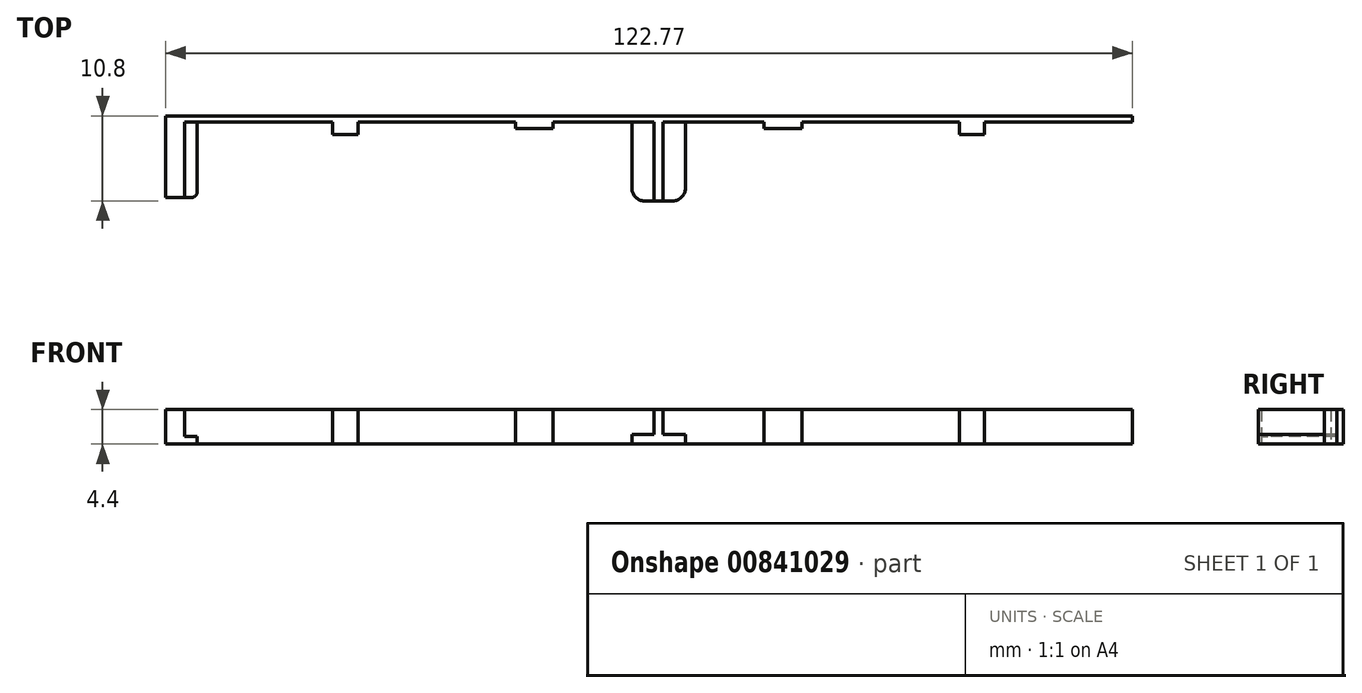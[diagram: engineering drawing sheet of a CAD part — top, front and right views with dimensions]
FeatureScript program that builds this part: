
annotation { "Feature Type Name" : "Feature", "Feature Type Description" : "" }
export const myFeature = defineFeature(function(context is Context, id is Id, definition is map)
    precondition{}
    {
        {
            var Q0;
            Q0=qCreatedBy(makeId("Top.planeOp"),FACE);
            var sketch = newSketch(context, id + "F0", { "sketchPlane" : qUnion([Q0])});
            skLineSegment(sketch, "E0", {"start": v(-62.6, 5.4) * mm, "end": v(62.6, 5.4) * mm});
            skLineSegment(sketch, "E1.top", {"start": v(-59.4, -4.2) * mm, "end": v(-62.6, -4.2) * mm});
            skLineSegment(sketch, "E1.left", {"start": v(-58.6, 6.2) * mm, "end": v(-58.6, -4.2) * mm});
            skLineSegment(sketch, "E1.right", {"start": v(-62.6, 6.2) * mm, "end": v(-62.6, -4.2) * mm});
            skLineSegment(sketch, "E2.bottom", {"start": v(-41.4, 5.4) * mm, "end": v(-38.2, 5.4) * mm});
            skLineSegment(sketch, "E2.top", {"start": v(-41.4, 3.8) * mm, "end": v(-38.2, 3.8) * mm});
            skLineSegment(sketch, "E2.left", {"start": v(-41.4, 5.4) * mm, "end": v(-41.4, 3.8) * mm});
            skLineSegment(sketch, "E2.right", {"start": v(-38.2, 5.4) * mm, "end": v(-38.2, 3.8) * mm});
            skLineSegment(sketch, "E3.bottom", {"start": v(-18.2, 5.4) * mm, "end": v(-13.4, 5.4) * mm});
            skLineSegment(sketch, "E3.top", {"start": v(-18.2, 4.6) * mm, "end": v(-13.4, 4.6) * mm});
            skLineSegment(sketch, "E3.left", {"start": v(-18.2, 5.4) * mm, "end": v(-18.2, 4.6) * mm});
            skLineSegment(sketch, "E3.right", {"start": v(-13.4, 5.4) * mm, "end": v(-13.4, 4.6) * mm});
            skLineSegment(sketch, "E4.bottom", {"start": v(3.4, 5.4) * mm, "end": v(-3.4, 5.4) * mm});
            skLineSegment(sketch, "E4.top", {"start": v(1.8, -4.6) * mm, "end": v(-1.8, -4.6) * mm});
            skLineSegment(sketch, "E4.left", {"start": v(3.4, 5.4) * mm, "end": v(3.4, -3) * mm});
            skLineSegment(sketch, "E4.right", {"start": v(-3.4, 5.4) * mm, "end": v(-3.4, -3) * mm});
            skPoint(sketch, "E4.middle", {"position": v(0, 0.4) * mm});
            skLineSegment(sketch, "E5.0", {"start": v(-60.2, 6.2) * mm, "end": v(-60.2, -4.2) * mm});
            skLineSegment(sketch, "E6", {"start": v(-62.6, 6.2) * mm, "end": v(62.6, 6.2) * mm});
            skPoint(sketch, "E7.visualSharp", {"position": v(-3.4, -4.6) * mm});
            skArc(sketch, "E7.filletArc", {"start": v(-3.4, -3) * mm, "mid": v(-2.93, -4.13) * mm, "end": v(-1.8, -4.6) * mm});
            skPoint(sketch, "E8.visualSharp", {"position": v(3.4, -4.6) * mm});
            skArc(sketch, "E8.filletArc", {"start": v(1.8, -4.6) * mm, "mid": v(2.93, -4.13) * mm, "end": v(3.4, -3) * mm});
            skLineSegment(sketch, "E9.0.left", {"start": v(-0.6, -4.6) * mm, "end": v(-0.6, 5.4) * mm});
            skLineSegment(sketch, "E9.0.right", {"start": v(0.6, -4.6) * mm, "end": v(0.6, 5.4) * mm});
            skArc(sketch, "E10.filletArc", {"start": v(-59.4, -4.2) * mm, "mid": v(-58.83, -3.97) * mm, "end": v(-58.6, -3.4) * mm});
            skLineSegment(sketch, "E11", {"start": v(62.6, 5.4) * mm, "end": v(62.6, 5.8) * mm});
            skLineSegment(sketch, "E12", {"start": v(62.6, 5.8) * mm, "end": v(62.6, 5.8) * mm});
            skLineSegment(sketch, "E13.MirrorCS", {"start": v(18.2, 4.6) * mm, "end": v(13.4, 4.6) * mm});
            skLineSegment(sketch, "E14.MirrorCS", {"start": v(18.2, 5.4) * mm, "end": v(18.2, 4.6) * mm});
            skLineSegment(sketch, "E15.MirrorCS", {"start": v(13.4, 5.4) * mm, "end": v(13.4, 4.6) * mm});
            skLineSegment(sketch, "E16.MirrorCS", {"start": v(38.2, 5.4) * mm, "end": v(38.2, 3.8) * mm});
            skLineSegment(sketch, "E17.MirrorCS", {"start": v(41.4, 5.4) * mm, "end": v(41.4, 3.8) * mm});
            skLineSegment(sketch, "E18.MirrorCS", {"start": v(41.4, 3.8) * mm, "end": v(38.2, 3.8) * mm});
            skLineSegment(sketch, "E19.MirrorCS", {"start": v(58.6, 6.2) * mm, "end": v(58.6, -4.2) * mm});
            skLineSegment(sketch, "E20.MirrorCS", {"start": v(60.17, 6.2) * mm, "end": v(60.2, -4.2) * mm});
            skLineSegment(sketch, "E21.MirrorCS", {"start": v(62.6, 6.2) * mm, "end": v(62.6, -4.2) * mm});
            skLineSegment(sketch, "E22.MirrorCS", {"start": v(59.4, -4.2) * mm, "end": v(62.6, -4.2) * mm});
            skArc(sketch, "E23.MirrorCS", {"start": v(59.4, -4.2) * mm, "mid": v(58.83, -3.97) * mm, "end": v(58.6, -3.4) * mm});
            skSolve(sketch);
        }
        {
            var Q0;
            {var subQ0=sQuery(id+"F0.wireOp",EDGE,"E1.right");var subQ1=sQuery(id+"F0.wireOp",EDGE,"E0");var subQ2=makeQuery(id+"F0.imprint","INTERSECT",VERTEX,{"derivedFrom":[subQ1,subQ0]});Q0=makeQuery(id+"F0.imprint","IMPRINT",FACE,{"disambiguationData":[TD([[makeQuery(id+"F0.imprint","IMPRINT",EDGE,{"disambiguationData":[TD([[subQ2,-1.0]])],"derivedFrom":subQ1}),-1.0]])]});}
            var Q1;
            {var subQ0=sQuery(id+"F0.wireOp",EDGE,"E1.right");var subQ1=sQuery(id+"F0.wireOp",EDGE,"E0");var subQ2=makeQuery(id+"F0.imprint","INTERSECT",VERTEX,{"derivedFrom":[subQ1,subQ0]});Q1=makeQuery(id+"F0.imprint","IMPRINT",FACE,{"disambiguationData":[TD([[makeQuery(id+"F0.imprint","IMPRINT",EDGE,{"disambiguationData":[TD([[subQ2,-1.0]])],"derivedFrom":subQ1}),1.0]])]});}
            var Q2;
            {var subQ17=sQuery(id+"F0.wireOp",EDGE,"E2.bottom");Q2=makeQuery(id+"F0.imprint","IMPRINT",FACE,{"disambiguationData":[TD([[makeQuery(id+"F0.imprint","IMPRINT",EDGE,{"derivedFrom":subQ17}),1.0]])]});}
            var Q3;
            {var subQ0=sQuery(id+"F0.wireOp",EDGE,"E21.MirrorCS");var subQ1=sQuery(id+"F0.wireOp",EDGE,"E0");var subQ2=makeQuery(id+"F0.imprint","INTERSECT",VERTEX,{"derivedFrom":[subQ1,subQ0]});Q3=makeQuery(id+"F0.imprint","IMPRINT",FACE,{"disambiguationData":[TD([[makeQuery(id+"F0.imprint","IMPRINT",EDGE,{"disambiguationData":[TD([[subQ2,1.0]])],"derivedFrom":subQ1}),1.0]])]});}
            var Q4;
            {var subQ0=sQuery(id+"F0.wireOp",EDGE,"E21.MirrorCS");var subQ1=sQuery(id+"F0.wireOp",EDGE,"E0");var subQ2=makeQuery(id+"F0.imprint","INTERSECT",VERTEX,{"derivedFrom":[subQ1,subQ0]});Q4=makeQuery(id+"F0.imprint","IMPRINT",FACE,{"disambiguationData":[TD([[makeQuery(id+"F0.imprint","IMPRINT",EDGE,{"disambiguationData":[TD([[subQ2,1.0]])],"derivedFrom":subQ1}),-1.0]])]});}
            var Q5;
            {var subQ0=sQuery(id+"F0.wireOp",EDGE,"E9.0.left");Q5=makeQuery(id+"F0.imprint","IMPRINT",FACE,{"disambiguationData":[TD([[makeQuery(id+"F0.imprint","IMPRINT",EDGE,{"derivedFrom":subQ0}),-1.0]])]});}
            var Q6;
            {var subQ0=sQuery(id+"F0.wireOp",EDGE,"E1.left");var subQ1=sQuery(id+"F0.wireOp",EDGE,"E0");var subQ2=makeQuery(id+"F0.imprint","INTERSECT",VERTEX,{"derivedFrom":[subQ1,subQ0]});Q6=makeQuery(id+"F0.imprint","IMPRINT",FACE,{"disambiguationData":[TD([[makeQuery(id+"F0.imprint","IMPRINT",EDGE,{"disambiguationData":[TD([[subQ2,1.0]])],"derivedFrom":subQ1}),1.0]])]});}
            var Q7;
            {var subQ0=sQuery(id+"F0.wireOp",EDGE,"E19.MirrorCS");var subQ1=sQuery(id+"F0.wireOp",EDGE,"E0");var subQ2=makeQuery(id+"F0.imprint","INTERSECT",VERTEX,{"derivedFrom":[subQ1,subQ0]});Q7=makeQuery(id+"F0.imprint","IMPRINT",FACE,{"disambiguationData":[TD([[makeQuery(id+"F0.imprint","IMPRINT",EDGE,{"disambiguationData":[TD([[subQ2,-1.0]])],"derivedFrom":subQ1}),1.0]])]});}
            extrude(context, id + "F1", {"entities" : qUnion([Q0, Q1, Q2, Q3, Q4, Q5, Q6, Q7]), "depth" : 4.4 * mm, "offsetDistance" : 25 * mm});
        }
        {
            var Q0;
            {var subQ0=sQuery(id+"F0.wireOp",EDGE,"E16.MirrorCS");Q0=makeQuery(id+"F0.imprint","IMPRINT",FACE,{"disambiguationData":[TD([[makeQuery(id+"F0.imprint","IMPRINT",EDGE,{"derivedFrom":subQ0}),1.0]])]});}
            var Q1;
            Q1=makeQuery(id+"F0.imprint","IMPRINT",FACE,{"disambiguationData":[TD([[makeQuery(id+"F0.imprint","IMPRINT",EDGE,{"derivedFrom":sQuery(id+"F0.wireOp",EDGE,"E13.MirrorCS")}),-1.0]])]});
            var Q2;
            {var subQ0=sQuery(id+"F0.wireOp",EDGE,"E4.left");Q2=makeQuery(id+"F0.imprint","IMPRINT",FACE,{"disambiguationData":[TD([[makeQuery(id+"F0.imprint","IMPRINT",EDGE,{"derivedFrom":subQ0}),-1.0]])]});}
            var Q3;
            {var subQ3=sQuery(id+"F0.wireOp",EDGE,"E4.right");Q3=makeQuery(id+"F0.imprint","IMPRINT",FACE,{"disambiguationData":[TD([[makeQuery(id+"F0.imprint","IMPRINT",EDGE,{"derivedFrom":subQ3}),1.0]])]});}
            var Q4;
            Q4=makeQuery(id+"F0.imprint","IMPRINT",FACE,{"disambiguationData":[TD([[makeQuery(id+"F0.imprint","IMPRINT",EDGE,{"derivedFrom":sQuery(id+"F0.wireOp",EDGE,"E3.bottom")}),-1.0]])]});
            var Q5;
            Q5=makeQuery(id+"F0.imprint","IMPRINT",FACE,{"disambiguationData":[TD([[makeQuery(id+"F0.imprint","IMPRINT",EDGE,{"derivedFrom":sQuery(id+"F0.wireOp",EDGE,"E2.bottom")}),-1.0]])]});
            extrude(context, id + "F2", {"entities" : qUnion([Q0, Q1, Q2, Q3, Q4, Q5]), "operationType" : NewBodyOperationType.ADD, "depth" : 1.2 * mm, "offsetDistance" : 25 * mm});
        }
        {
            var Q0;
            {var subQ5=sQuery(id+"F0.wireOp",EDGE,"E10.filletArc");Q0=makeQuery(id+"F0.imprint","IMPRINT",FACE,{"disambiguationData":[TD([[makeQuery(id+"F0.imprint","IMPRINT",EDGE,{"derivedFrom":subQ5}),1.0]])]});}
            var Q1;
            {var subQ3=sQuery(id+"F0.wireOp",EDGE,"E23.MirrorCS");Q1=makeQuery(id+"F0.imprint","IMPRINT",FACE,{"disambiguationData":[TD([[makeQuery(id+"F0.imprint","IMPRINT",EDGE,{"derivedFrom":subQ3}),-1.0]])]});}
            extrude(context, id + "F3", {"entities" : qUnion([Q0, Q1]), "operationType" : NewBodyOperationType.ADD, "depth" : 1 * mm, "offsetDistance" : 25 * mm});
        }
    });
